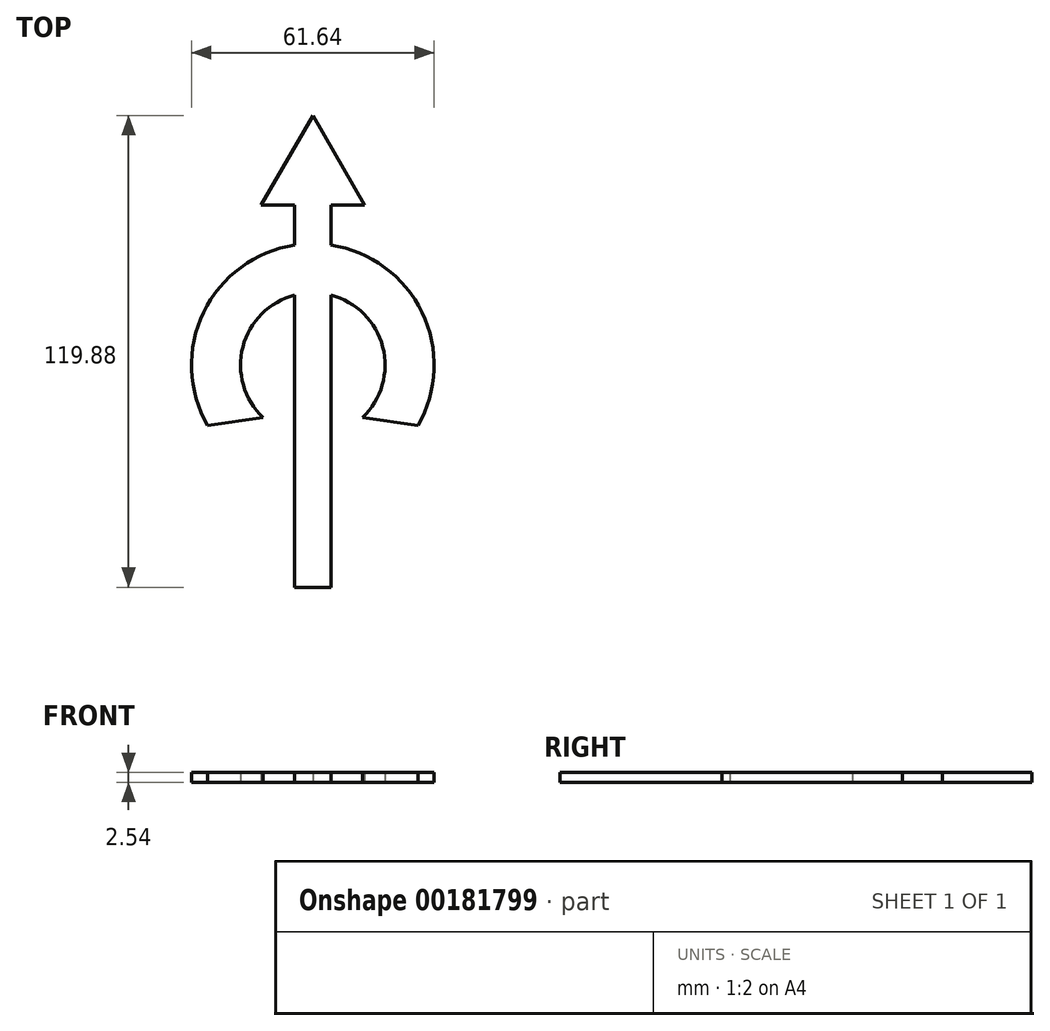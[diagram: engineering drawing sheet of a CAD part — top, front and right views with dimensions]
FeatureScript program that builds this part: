
annotation { "Feature Type Name" : "Feature", "Feature Type Description" : "" }
export const myFeature = defineFeature(function(context is Context, id is Id, definition is map)
    precondition{}
    {
        {
            var Q0;
            Q0=qCreatedBy(makeId("Top.planeOp"),FACE);
            var sketch = newSketch(context, id + "F0", { "sketchPlane" : qUnion([Q0])});
            skLineSegment(sketch, "E0.top", {"start": v(-4.57, -56.48) * mm, "end": v(4.57, -56.48) * mm});
            skPoint(sketch, "E1", {"position": v(4.57, 30.48) * mm});
            skPoint(sketch, "E2", {"position": v(4.57, 17.78) * mm});
            skLineSegment(sketch, "E3.trimOffspring", {"start": v(4.57, 17.78) * mm, "end": v(4.57, -56.48) * mm});
            skArc(sketch, "E4", {"start": v(4.57, 17.78) * mm, "mid": v(14.5, 11.25) * mm, "end": v(18.36, 0) * mm});
            skArc(sketch, "E5", {"start": v(4.57, 30.48) * mm, "mid": v(23.35, 20.11) * mm, "end": v(30.82, 0) * mm});
            skArc(sketch, "E6", {"start": v(18.36, 0) * mm, "mid": v(16.87, -7.25) * mm, "end": v(12.63, -13.32) * mm});
            skArc(sketch, "E7", {"start": v(30.82, 0) * mm, "mid": v(29.77, -7.97) * mm, "end": v(26.7, -15.4) * mm});
            skLineSegment(sketch, "E8", {"start": v(12.63, -13.32) * mm, "end": v(26.7, -15.4) * mm});
            skPoint(sketch, "E9", {"position": v(-4.57, 30.48) * mm});
            skPoint(sketch, "E10", {"position": v(-4.57, 17.78) * mm});
            skArc(sketch, "E11", {"start": v(-4.57, 30.48) * mm, "mid": v(-27.76, 13.39) * mm, "end": v(-26.7, -15.4) * mm});
            skArc(sketch, "E12", {"start": v(-4.57, 17.78) * mm, "mid": v(-17.77, 4.6) * mm, "end": v(-12.63, -13.33) * mm});
            skLineSegment(sketch, "E13", {"start": v(-26.7, -15.4) * mm, "end": v(-12.63, -13.33) * mm});
            skLineSegment(sketch, "E14.0", {"start": v(13.13, 40.66) * mm, "end": v(4.57, 40.66) * mm});
            skLineSegment(sketch, "E14.1", {"start": v(-13.13, 40.66) * mm, "end": v(0, 63.4) * mm});
            skLineSegment(sketch, "E14.2", {"start": v(0, 63.4) * mm, "end": v(13.13, 40.66) * mm});
            skPoint(sketch, "E14.0.midPoint", {"position": v(0, 40.66) * mm});
            skLineSegment(sketch, "E15.trimOffspring", {"start": v(-4.57, 17.78) * mm, "end": v(-4.57, -56.48) * mm});
            skLineSegment(sketch, "E16.trimOffspring", {"start": v(-4.57, 40.66) * mm, "end": v(-4.57, 30.48) * mm});
            skLineSegment(sketch, "E17.trimOffspring", {"start": v(4.57, 40.66) * mm, "end": v(4.57, 30.48) * mm});
            skPoint(sketch, "E14.cCircle.center.orphan", {"position": v(0, 48.24) * mm});
            skLineSegment(sketch, "E18.trimOffspring", {"start": v(-4.57, 40.66) * mm, "end": v(-13.13, 40.66) * mm});
            skSolve(sketch);
        }
        {
            var Q0;
            Q0 = qSketchRegion(id + "F0", true);
            extrude(context, id + "F1", {"entities" : qUnion([Q0]), "depth" : 2.54 * mm});
        }
    });
